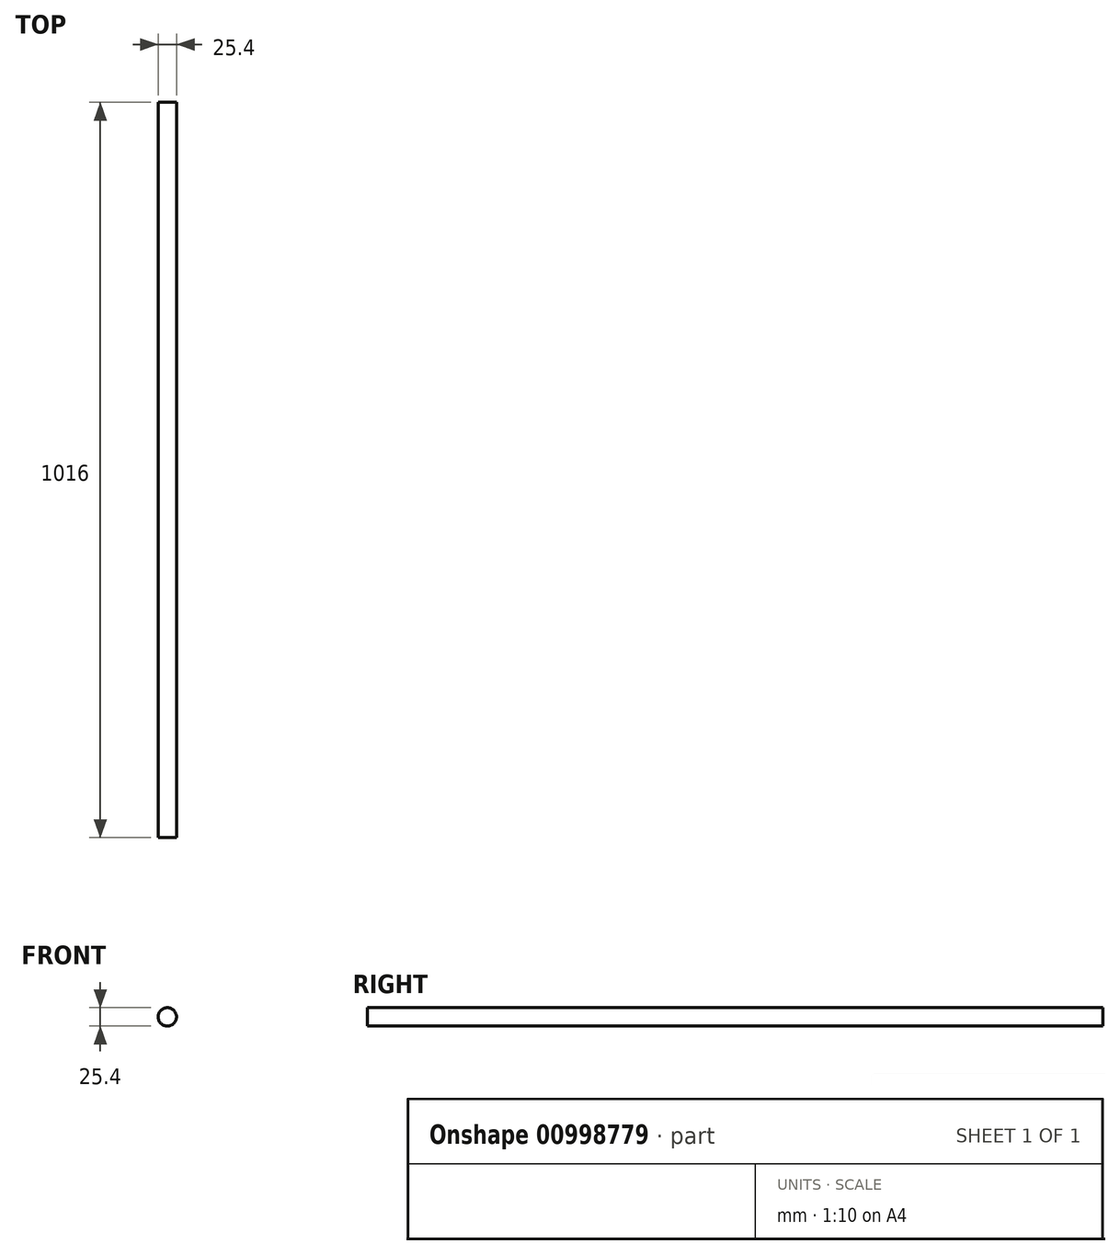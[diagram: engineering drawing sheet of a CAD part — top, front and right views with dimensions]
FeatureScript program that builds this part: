
annotation { "Feature Type Name" : "Feature", "Feature Type Description" : "" }
export const myFeature = defineFeature(function(context is Context, id is Id, definition is map)
    precondition{}
    {
        {
            var Q0;
            Q0=qCreatedBy(makeId("Front.planeOp"),FACE);
            var sketch = newSketch(context, id + "F0", { "sketchPlane" : qUnion([Q0])});
            skCircle(sketch, "E0", {"center": v(1.94, 0) * mm, "radius": 12.7 * mm});
            skSolve(sketch);
        }
        {
            var Q0;
            Q0=makeQuery(id+"F0.imprint","IMPRINT",FACE,{"disambiguationData":[TD([[makeQuery(id+"F0.imprint","IMPRINT",EDGE,{"derivedFrom":sQuery(id+"F0.wireOp",EDGE,"E0")}),1.0]])]});
            extrude(context, id + "F1", {"entities" : qUnion([Q0]), "depth" : 1016 * mm, "offsetDistance" : 25.4 * mm});
        }
    });
